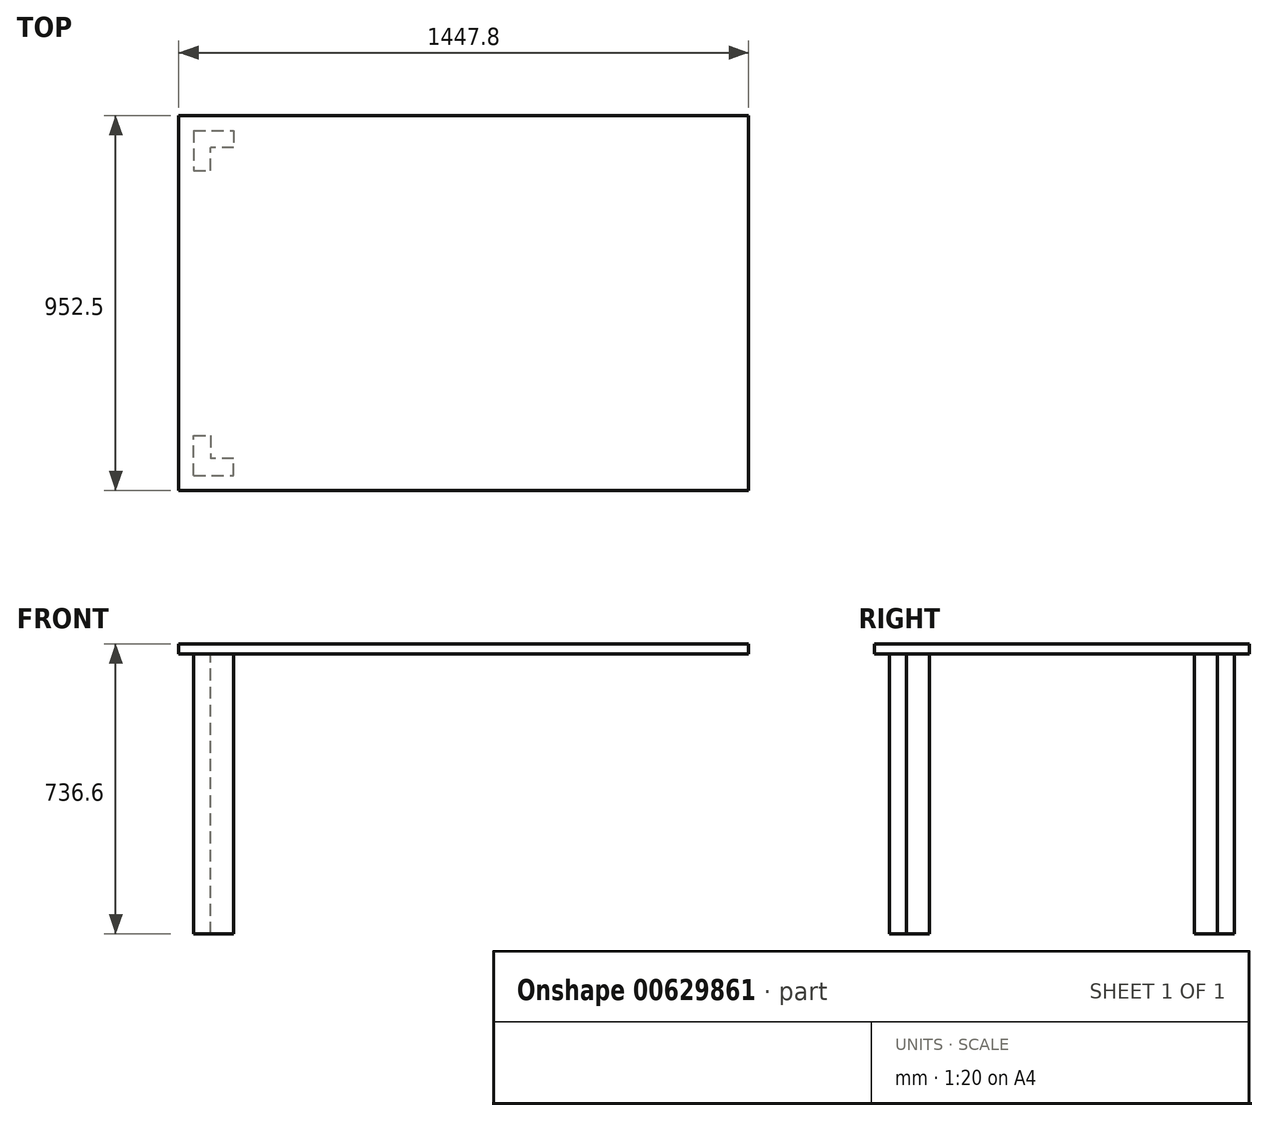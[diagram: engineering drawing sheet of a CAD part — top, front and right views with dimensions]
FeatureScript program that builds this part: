
annotation { "Feature Type Name" : "Feature", "Feature Type Description" : "" }
export const myFeature = defineFeature(function(context is Context, id is Id, definition is map)
    precondition{}
    {
        {
            var Q0;
            Q0=qCreatedBy(makeId("Top.planeOp"),FACE);
            var sketch = newSketch(context, id + "F0", { "sketchPlane" : qUnion([Q0])});
            skLineSegment(sketch, "E0.bottom", {"start": v(-1447.8, -476.25) * mm, "end": v(0, -476.25) * mm});
            skLineSegment(sketch, "E0.top", {"start": v(-1447.8, 476.25) * mm, "end": v(0, 476.25) * mm});
            skLineSegment(sketch, "E0.left", {"start": v(-1447.8, -476.25) * mm, "end": v(-1447.8, 476.25) * mm});
            skLineSegment(sketch, "E1.bottom", {"start": v(-1409.7, 438.15) * mm, "end": v(-1308.1, 438.15) * mm});
            skLineSegment(sketch, "E1.top", {"start": v(-1409.7, 336.55) * mm, "end": v(-1366.28, 336.55) * mm});
            skLineSegment(sketch, "E1.left", {"start": v(-1409.7, 438.15) * mm, "end": v(-1409.7, 336.55) * mm});
            skLineSegment(sketch, "E1.right", {"start": v(-1308.1, 438.15) * mm, "end": v(-1308.1, 394.73) * mm});
            skLineSegment(sketch, "E2.top", {"start": v(-1308.1, 394.73) * mm, "end": v(-1366.28, 394.73) * mm});
            skLineSegment(sketch, "E2.right", {"start": v(-1366.28, 336.55) * mm, "end": v(-1366.28, 394.73) * mm});
            skLineSegment(sketch, "E3", {"start": v(0, 0) * mm, "end": v(-1447.8, 0) * mm, "construction": true});
            skLineSegment(sketch, "E4", {"start": v(0, 476.25) * mm, "end": v(0, -476.25) * mm});
            skSolve(sketch);
        }
        {
            var Q0;
            Q0=makeQuery(id+"F0.imprint","IMPRINT",FACE,{"disambiguationData":[TD([[makeQuery(id+"F0.imprint","IMPRINT",EDGE,{"derivedFrom":sQuery(id+"F0.wireOp",EDGE,"E1.bottom")}),-1.0]])]});
            extrude(context, id + "F1", {"entities" : qUnion([Q0]), "oppositeDirection" : true, "depth" : 736.6 * mm, "offsetDistance" : 25.4 * mm});
        }
        {
            var Q0;
            Q0=makeQuery(id+"F1.opExtrude","SWEPT_BODY",BODY,{"disambiguationData":[OSD([sQuery(id+"F0.wireOp",EDGE,"E1.bottom"),sQuery(id+"F0.wireOp",EDGE,"E1.top"),sQuery(id+"F0.wireOp",EDGE,"E1.left"),sQuery(id+"F0.wireOp",EDGE,"E1.right"),sQuery(id+"F0.wireOp",EDGE,"E2.top"),sQuery(id+"F0.wireOp",EDGE,"E2.right")])]});
            var Q1;
            Q1=qCreatedBy(makeId("Front.planeOp"),FACE);
            mirror(context, id + "F2", {"entities" : qUnion([Q0]), "mirrorPlane" : qUnion([Q1])});
        }
        {
            var Q0;
            Q0=makeQuery(id+"F0.imprint","IMPRINT",FACE,{"disambiguationData":[TD([[makeQuery(id+"F0.imprint","IMPRINT",EDGE,{"derivedFrom":sQuery(id+"F0.wireOp",EDGE,"E0.bottom")}),1.0]])]});
            extrude(context, id + "F3", {"entities" : qUnion([Q0]), "operationType" : NewBodyOperationType.ADD, "oppositeDirection" : true, "depth" : 25.4 * mm, "offsetDistance" : 25.4 * mm});
        }
    });
